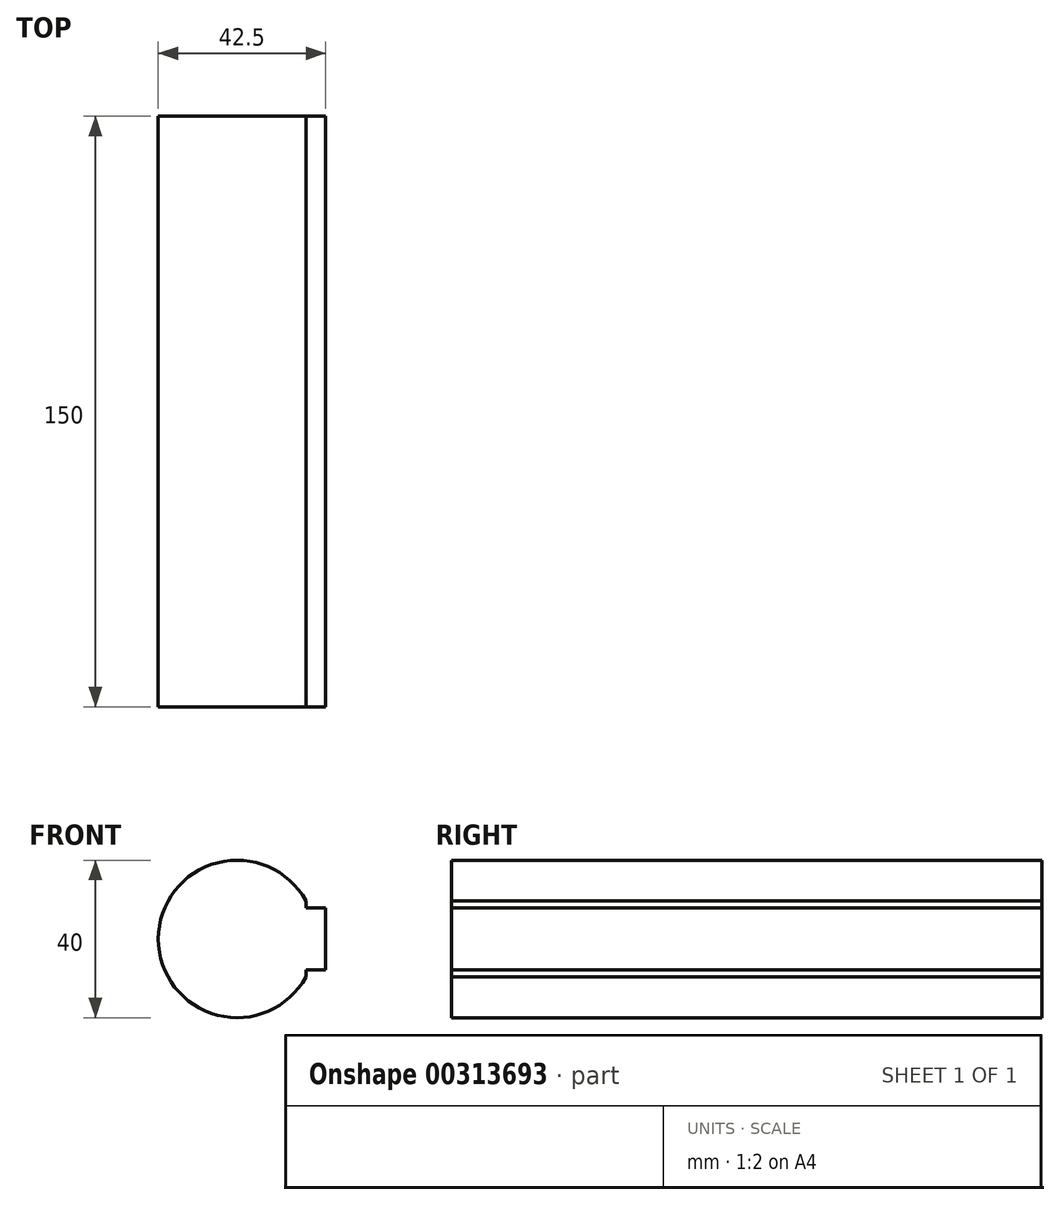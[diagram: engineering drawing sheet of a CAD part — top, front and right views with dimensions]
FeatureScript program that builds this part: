
annotation { "Feature Type Name" : "Feature", "Feature Type Description" : "" }
export const myFeature = defineFeature(function(context is Context, id is Id, definition is map)
    precondition{}
    {
        {
            var Q0;
            Q0=qCreatedBy(makeId("Front.planeOp"),FACE);
            var sketch = newSketch(context, id + "F0", { "sketchPlane" : qUnion([Q0])});
            skArc(sketch, "E0", {"start": v(17.5, 9.68) * mm, "mid": v(-20, 0) * mm, "end": v(17.5, -9.68) * mm});
            skPoint(sketch, "E1", {"position": v(20, 0) * mm});
            skLineSegment(sketch, "E2.bottom", {"start": v(22.5, 7.84) * mm, "end": v(17.5, 7.84) * mm});
            skLineSegment(sketch, "E2.top", {"start": v(22.5, -7.84) * mm, "end": v(17.5, -7.84) * mm});
            skLineSegment(sketch, "E2.left", {"start": v(22.5, 7.84) * mm, "end": v(22.5, -7.84) * mm});
            skLineSegment(sketch, "E2.right", {"start": v(17.5, 9.68) * mm, "end": v(17.5, 7.84) * mm});
            skLineSegment(sketch, "E3.trimOffspring", {"start": v(17.5, -7.84) * mm, "end": v(17.5, -9.68) * mm});
            skSolve(sketch);
        }
        {
            var Q0;
            Q0=qSketchRegion(id+"F0",true);
            extrude(context, id + "F1", {"entities" : qUnion([Q0]), "endBound" : BoundingType.SYMMETRIC, "depth" : 150 * mm});
        }
    });
